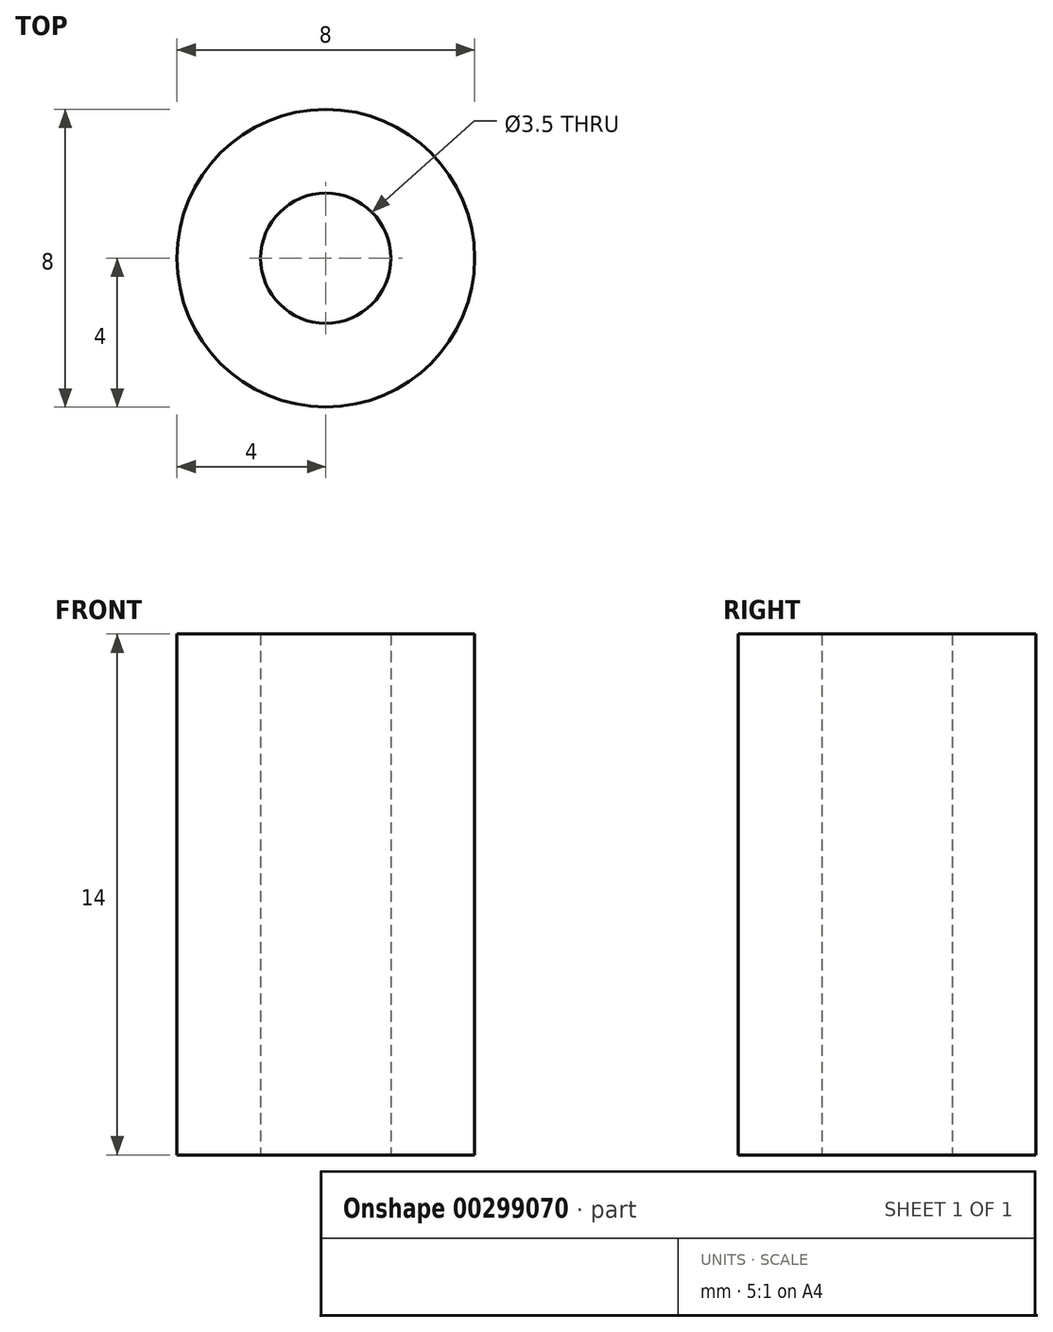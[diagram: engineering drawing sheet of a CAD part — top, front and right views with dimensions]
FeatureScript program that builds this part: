
annotation { "Feature Type Name" : "Feature", "Feature Type Description" : "" }
export const myFeature = defineFeature(function(context is Context, id is Id, definition is map)
    precondition{}
    {
        {
            var Q0;
            Q0=qCreatedBy(makeId("Top.planeOp"),FACE);
            var sketch = newSketch(context, id + "F0", { "sketchPlane" : qUnion([Q0])});
            skCircle(sketch, "E0", {"center": v(0, 0) * mm, "radius": 1.75 * mm});
            skCircle(sketch, "E1", {"center": v(0, 0) * mm, "radius": 4 * mm});
            skSolve(sketch);
        }
        {
            var Q0;
            Q0 = qSketchRegion(id + "F0", true);
            var Q1;
            Q1=makeQuery(id+"F0.imprint","IMPRINT",FACE,{"disambiguationData":[TD([[makeQuery(id+"F0.imprint","IMPRINT",EDGE,{"derivedFrom":sQuery(id+"F0.wireOp",EDGE,"E0")}),-1.0]])]});
            extrude(context, id + "F1", {"entities" : qUnion([Q0, Q1]), "depth" : 14 * mm});
        }
    });
